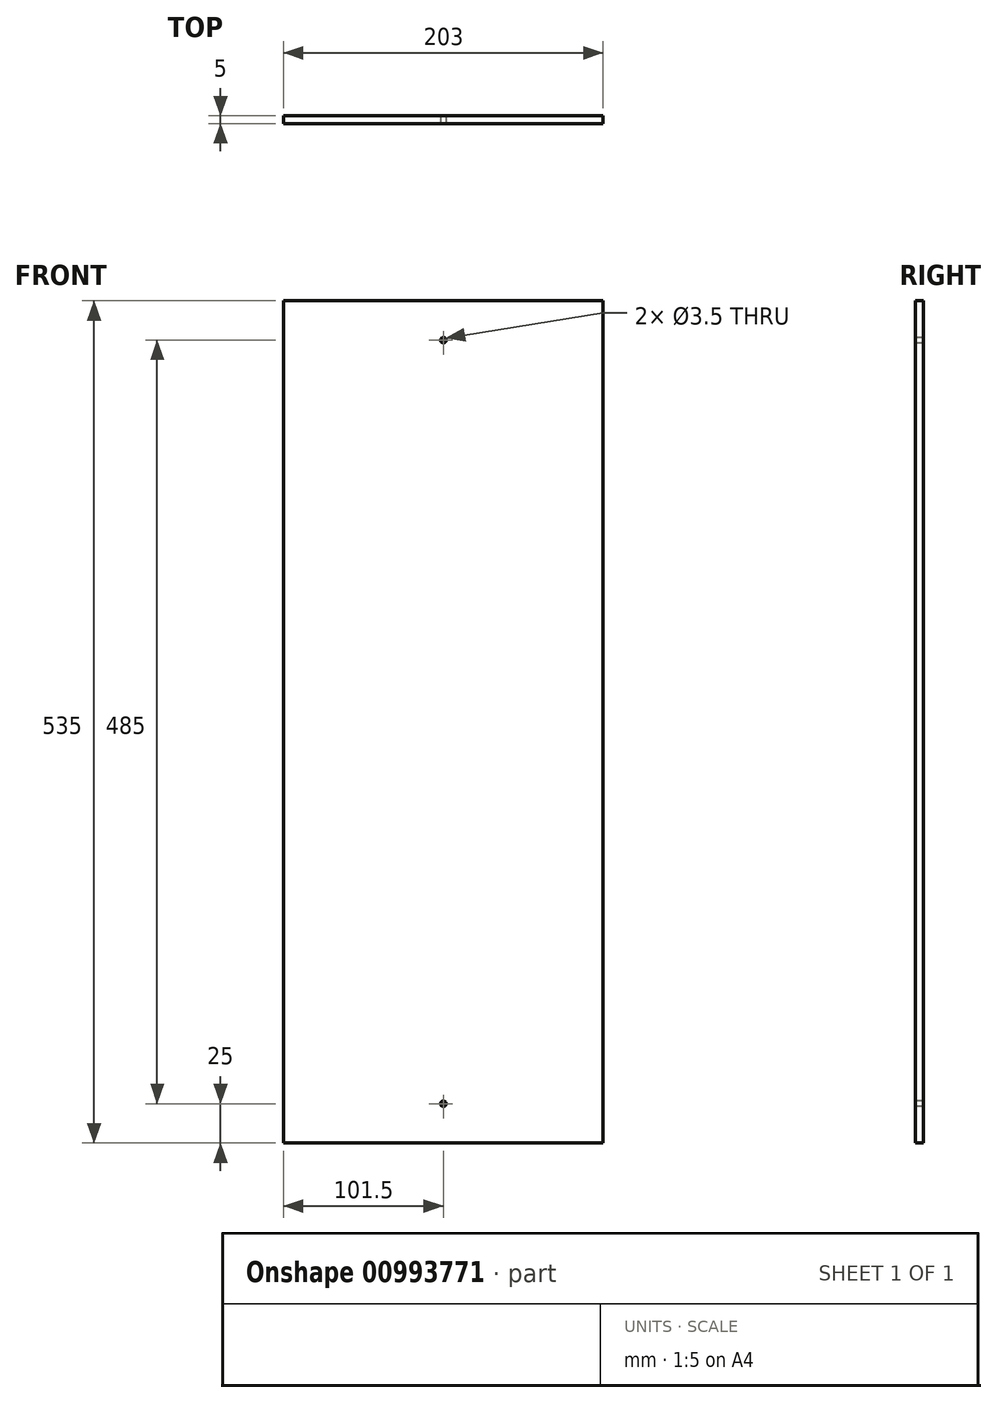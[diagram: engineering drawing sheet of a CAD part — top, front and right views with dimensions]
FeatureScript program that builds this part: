
annotation { "Feature Type Name" : "Feature", "Feature Type Description" : "" }
export const myFeature = defineFeature(function(context is Context, id is Id, definition is map)
    precondition{}
    {
        {
            var Q0;
            Q0=qCreatedBy(makeId("Front.planeOp"),FACE);
            var sketch = newSketch(context, id + "F0", { "sketchPlane" : qUnion([Q0])});
            skLineSegment(sketch, "E0.bottom", {"start": v(0, 0) * mm, "end": v(203, 0) * mm});
            skLineSegment(sketch, "E0.top", {"start": v(0, 535) * mm, "end": v(203, 535) * mm});
            skLineSegment(sketch, "E0.left", {"start": v(0, 0) * mm, "end": v(0, 535) * mm});
            skLineSegment(sketch, "E0.right", {"start": v(203, 0) * mm, "end": v(203, 535) * mm});
            skSolve(sketch);
        }
        {
            var Q0;
            Q0=makeQuery(id+"F0.imprint","IMPRINT",FACE,{"disambiguationData":[TD([[makeQuery(id+"F0.imprint","IMPRINT",EDGE,{"derivedFrom":sQuery(id+"F0.wireOp",EDGE,"E0.bottom")}),1.0]])]});
            extrude(context, id + "F1", {"entities" : qUnion([Q0]), "oppositeDirection" : true, "depth" : 5 * mm, "offsetDistance" : 25 * mm});
        }
        {
            var Q0;
            Q0=makeQuery(id+"F1.opExtrude","CAP_FACE",FACE,{"disambiguationData":[OSD([sQuery(id+"F0.wireOp",EDGE,"E0.bottom"),sQuery(id+"F0.wireOp",EDGE,"E0.top"),sQuery(id+"F0.wireOp",EDGE,"E0.left"),sQuery(id+"F0.wireOp",EDGE,"E0.right")])],"isStart":true});
            var sketch = newSketch(context, id + "F2", { "sketchPlane" : qUnion([Q0])});
            skCircle(sketch, "E1", {"center": v(101.5, 510) * mm, "radius": 1.75 * mm});
            skPoint(sketch, "E1.centerSnap0", {"position": v(101.5, 535) * mm});
            skCircle(sketch, "E2", {"center": v(101.5, 25) * mm, "radius": 1.75 * mm});
            skPoint(sketch, "E2.centerSnap0", {"position": v(101.5, 0) * mm});
            skSolve(sketch);
        }
        {
            var Q0;
            Q0 = qSketchRegion(id + "F2", true);
            extrude(context, id + "F3", {"entities" : qUnion([Q0]), "operationType" : NewBodyOperationType.REMOVE, "oppositeDirection" : true, "depth" : 25 * mm, "offsetDistance" : 25 * mm});
        }
    });
